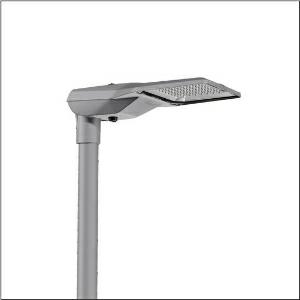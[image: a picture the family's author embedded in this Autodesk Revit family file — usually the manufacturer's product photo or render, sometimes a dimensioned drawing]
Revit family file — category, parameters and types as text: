
# Revit family: streetlight_sl_21_midi___st1_5a_5xe3p33t08mb_b96f
name_source: partatom
category: Lighting Fixtures
units: mm (PartAtom-declared; Revit-internal decimal feet)

## family parameters
Cut with Voids When Loaded = No
Host = Face
Light Source = No
Part Type = Normal
Room Calculation Point = No
Round Connector Dimension = Use Diameter
Shared = No

## types (1)
- --- (1 x LED, 17960 lm, 136 W, 3000K)
    Apparent Load = 136 VA
    CIE Flux Codes = 22 53 95 100 100
    Color Rendering = 70
    Color Temperature = 3000K
    Default Elevation = 1800 mm
    Description = Streetlight SL 21 midi, mast luminaire, primary light control with lens, of PMMA, primary optical cover: cover, of toughened safety glass, transparent, light distribution: ST1.5a, light emission: direct distribution, primary light characteristic: asymmetric, installation type: side-entry, post-top, LED, High Power LED, rated luminous flux: 17.960lm, luminous efficacy: 132lm/W, light colour: 730, colour temperature: 3000K, control gear: D4i, control: overheat protection, constant luminous flux control, time-dependent luminous flux control, flexible luminous flux parameterisation, pre-setting: logarithmic dimming characteristic, mains connection: 230..240V, AC, 50/60Hz, start of lifetime: 136W, end of service life: 142W, reduction: 61W, luminaire housing, of diecast aluminium, powder-coated, SITECO metallic grey (DB 702S), corrosivity category C5 high according to DIN EN ISO 12944, please order mast flange separately, inclination adjustable: 0°, 5°, 10°, 15°, sealing non-destructively replaceable, multi-level sealing system, length: 644mm, width: 335mm, height: 110mm, mast flange for spigot size: 42mm (side-entry): 5XC10008XM4, 60/48mm (side-entry/post-top): 5XC10108XM2, 76/60mm (side-entry/post-top): 5XC10108XM1, mounting height: 4..8m, Smart Interface below and above, protection rating (complete): IP66, insulation class (complete): insulation class II (safety insulation), certification: CE, ENEC, ENEC+, VDE, impact resistance: IK10, permissible operating ambient temperature for outdoor applications: -40..+50°C, standard-compliant lighting for roads and squares, packaging unit: 1 piece

Light Distribution: ST1.5a
    Height = 111 mm
    Lamp = 1 x LED
    Lamp Light Flux = 17960 lm
    Lamp Power = 136 W
    Lamp count = 1
    Length = 644 mm
    Luminous efficacy = 132 lm/W
    Manufacturer = Siteco
    ModVariant = No
    Model = 5XE3P33T08MB
    Number of Poles = 1
    OnlyDefault = Yes
    Power Factor = 1
    Product Name = Streetlight SL 21 midi | ST1.5a
    Product group = mast luminaire | pylon top
    ProductGroupID = 6100
    Protection Class = Protection class II
    Protection Degree = IP 66
    RLX_Detail_Level = 1
    RLX_Emergency_Light_Flux = 0 lm
    RLX_Emergency_Type = 0
    RLX_Emergency_Type_DB = No
    RlxData = <blob elided: 30553 chars, md5=ab4b1f35>
    Socket = socket
    Standby Power = 0 W
    System Light Flux = 17960 lm
    System Power = 136 W
    Type Comments = factory setting: luminous flux: 100 % | dim-lin: 254 | 695 mA
    Type Image = l_1004304.jpg
    URL = http://relux.com
    VarID = @adj_175583
    Voltage = 0 V
    Weight = 0.00 kg
    Width = 336 mm

## geometry (parser evidence)
native form markers: Blend x4, Sweep x10
no freeform markers — native parametric forms only
